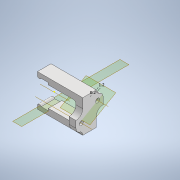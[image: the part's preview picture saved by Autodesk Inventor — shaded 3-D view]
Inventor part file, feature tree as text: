
AUTODESK INVENTOR PART (.ipt)
format: ipt  version: 2021 (Build 250183000, 183)  size: 239,104 bytes
history: native  units: in
note: dims shown in document units (in); Inventor stores cm internally (conversion verified against a paired STEP export)
features: other x7, sketch x6, extrude x4, fillet x4, plane x2, reference x2, projected_geometry x2, hole x1
ambient origin geometry x8: Origin, YZ Plane, XZ Plane, XY Plane, X Axis, Y Axis, Z Axis, Center Point
bodies: Body1 (feature_tree)
feature tree (28):
  other  "Work Axis2"
  extrude  "Extrusion3"  Depth=0.1181in
  extrude  "Extrusion4"  Depth=0.3937in TaperAngle=0.0deg
  hole  "Hole1"  [1 undecoded]
  extrude  "Extrusion5"  Depth=0.3937in TaperAngle=0.0deg
  plane  "Work Plane1"
  other  "Work Axis3"
  other  "Work Axis4"
  plane  "Work Plane2"
  sketch  "Sketch7"  dims[d22=0.1181in d23=0.2362in d24=0.1575in d25=0.0787in d26=90.0deg d27=0.315in d28=0.8108in d29=0.1969in d30=0.1378in d31=0.0in d32=0.0079in d33=0.0472in d34=0.0315in]
  extrude  "Extrusion6"  Depth=0.1969in
  fillet  "Fillet2"  Radius=0.1378in
  fillet  "Fillet3"  Radius=0.0079in
  fillet  "Fillet4"  Radius=0.0472in
  fillet  "Fillet5"  Radius=0.0315in
  sketch  "Sketch3"  dims[d11=0.1181in d12=0.1181in]
  sketch  "Sketch4"  dims[d13=0.1772in d15=0.3937in d16=0.0in]
  sketch  "Sketch5"  dims[d17=0.7874in d18=0.1181in]
  reference  "Reference17"
  reference  "Reference18"
  sketch  "Sketch6"  dims[d19=0.1181in d20=0.3937in d21=0.0in]
  projected_geometry  "Projected Loop1"
  projected_geometry  "Projected Loop2"
  sketch  "Sketch8"  dims[d35=0.1102in d37=0.3937in d38=0.0in d40=0.3543in d41=0.3543in d42=0.1969in d43=0.1575in d44=0.1181in d45=0.0787in d47=0.1969in d48=0.3543in d49=0.3543in d50=0.1969in d51=1.3154in d52=0.1969in d5=0.0197in d6=0.0344in d7=0.0197in d8=0.0344in d36=0.0197in d39=0.0344in]
  other  "assy_gic_kinematic_2d_robot_arm_MK1_v2.iam"
  other  "Pololu 1-2in Ball caster:1"
  other  "sub_assy_robot_arm_link1:1"
  other  "arm_1_v2:1"
note: 1 required parameter value undecoded (feature->parameter linkage not recoverable at this tier; creation-order binding heuristic only, values carry confidence <= 0.55)
